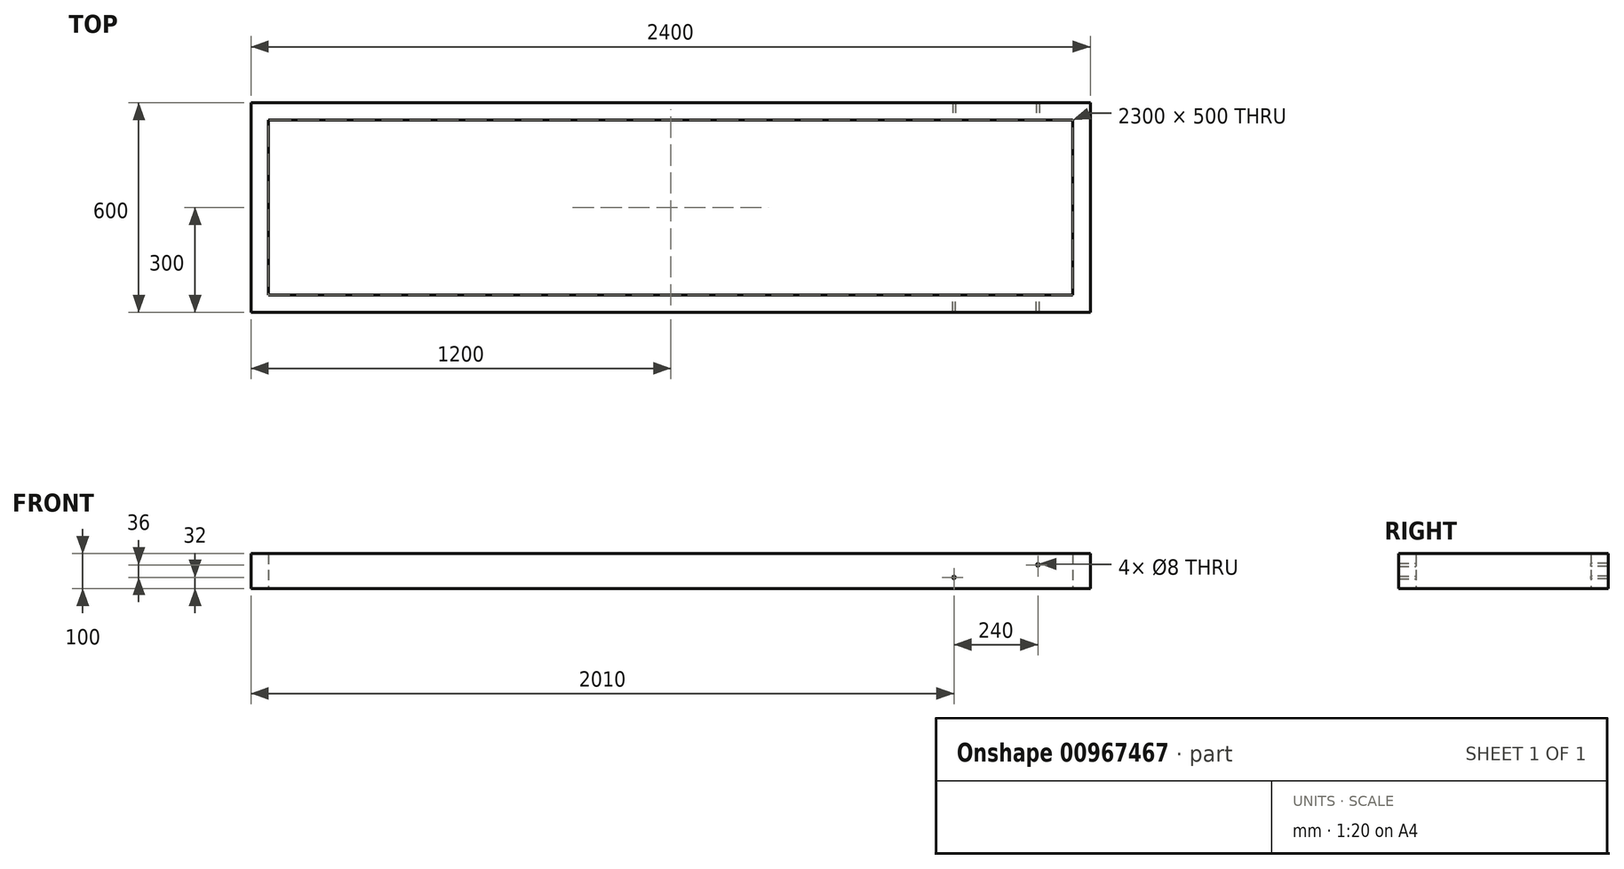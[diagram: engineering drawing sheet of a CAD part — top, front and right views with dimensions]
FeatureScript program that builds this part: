
annotation { "Feature Type Name" : "Feature", "Feature Type Description" : "" }
export const myFeature = defineFeature(function(context is Context, id is Id, definition is map)
    precondition{}
    {
        {
            var Q0;
            Q0=qCreatedBy(makeId("Top.planeOp"),FACE);
            var sketch = newSketch(context, id + "F0", { "sketchPlane" : qUnion([Q0])});
            skLineSegment(sketch, "E0.bottom", {"start": v(1200, -300) * mm, "end": v(-1200, -300) * mm});
            skLineSegment(sketch, "E0.top", {"start": v(1200, 300) * mm, "end": v(-1200, 300) * mm});
            skLineSegment(sketch, "E0.left", {"start": v(1200, -300) * mm, "end": v(1200, 300) * mm});
            skLineSegment(sketch, "E0.right", {"start": v(-1200, -300) * mm, "end": v(-1200, 300) * mm});
            skPoint(sketch, "E0.middle", {"position": v(0, 0) * mm});
            skLineSegment(sketch, "E1.bottom", {"start": v(1150, -250) * mm, "end": v(-1150, -250) * mm});
            skLineSegment(sketch, "E1.top", {"start": v(1150, 250) * mm, "end": v(-1150, 250) * mm});
            skLineSegment(sketch, "E1.left", {"start": v(1150, -250) * mm, "end": v(1150, 250) * mm});
            skLineSegment(sketch, "E1.right", {"start": v(-1150, -250) * mm, "end": v(-1150, 250) * mm});
            skSolve(sketch);
        }
        {
            var Q0;
            Q0=makeQuery(id+"F0.imprint","IMPRINT",FACE,{"disambiguationData":[TD([[makeQuery(id+"F0.imprint","IMPRINT",EDGE,{"derivedFrom":sQuery(id+"F0.wireOp",EDGE,"E0.bottom")}),-1.0]])]});
            extrude(context, id + "F1", {"entities" : qUnion([Q0]), "depth" : 100 * mm, "offsetDistance" : 25 * mm});
        }
        {
            var Q0;
            Q0=makeQuery(id+"F1.opExtrude","SWEPT_FACE",FACE,{"disambiguationData":[OSD([sQuery(id+"F0.wireOp",EDGE,"E1.top")])]});
            var sketch = newSketch(context, id + "F2", { "sketchPlane" : qUnion([Q0])});
            skCircle(sketch, "E2", {"center": v(1050, 68) * mm, "radius": 4 * mm});
            skCircle(sketch, "E3", {"center": v(810, 32) * mm, "radius": 4 * mm});
            skSolve(sketch);
        }
        {
            var Q0;
            Q0=makeQuery(id+"F2.imprint","IMPRINT",FACE,{"disambiguationData":[TD([[makeQuery(id+"F2.imprint","IMPRINT",EDGE,{"derivedFrom":sQuery(id+"F2.wireOp",EDGE,"E3")}),1.0]])]});
            var Q1;
            Q1=makeQuery(id+"F2.imprint","IMPRINT",FACE,{"disambiguationData":[TD([[makeQuery(id+"F2.imprint","IMPRINT",EDGE,{"derivedFrom":sQuery(id+"F2.wireOp",EDGE,"E2")}),1.0]])]});
            var Q2;
            Q2=makeQuery(id+"F1.opExtrude","SWEPT_FACE",FACE,{"disambiguationData":[OSD([sQuery(id+"F0.wireOp",EDGE,"E0.top")])]});
            var Q3;
            Q3=makeQuery(id+"F1.opExtrude","SWEPT_FACE",FACE,{"disambiguationData":[OSD([sQuery(id+"F0.wireOp",EDGE,"E0.bottom")])]});
            var Q4;
            Q4=makeQuery(id+"F1.opExtrude","SWEPT_BODY",BODY,{"disambiguationData":[OSD([sQuery(id+"F0.wireOp",EDGE,"E0.bottom"),sQuery(id+"F0.wireOp",EDGE,"E0.top"),sQuery(id+"F0.wireOp",EDGE,"E0.left"),sQuery(id+"F0.wireOp",EDGE,"E0.right"),sQuery(id+"F0.wireOp",EDGE,"E1.bottom"),sQuery(id+"F0.wireOp",EDGE,"E1.top"),sQuery(id+"F0.wireOp",EDGE,"E1.left"),sQuery(id+"F0.wireOp",EDGE,"E1.right")])]});
            extrude(context, id + "F3", {"entities" : qUnion([Q0, Q1]), "operationType" : NewBodyOperationType.REMOVE, "endBound" : BoundingType.UP_TO_NEXT, "oppositeDirection" : true, "depth" : 25 * mm, "endBoundEntityFace" : qUnion([Q2]), "offsetDistance" : 25 * mm});
        }
        {
            var Q0;
            Q0=makeQuery(id+"F1.opExtrude","SWEPT_FACE",FACE,{"disambiguationData":[OSD([sQuery(id+"F0.wireOp",EDGE,"E1.bottom")])]});
            var sketch = newSketch(context, id + "F4", { "sketchPlane" : qUnion([Q0])});
            skCircle(sketch, "E4", {"center": v(-1050, 68) * mm, "radius": 4 * mm});
            skCircle(sketch, "E5", {"center": v(-810, 32) * mm, "radius": 4 * mm});
            skSolve(sketch);
        }
        {
            var Q0;
            Q0=makeQuery(id+"F4.imprint","IMPRINT",FACE,{"disambiguationData":[TD([[makeQuery(id+"F4.imprint","IMPRINT",EDGE,{"derivedFrom":sQuery(id+"F4.wireOp",EDGE,"E5")}),1.0]])]});
            var Q1;
            Q1=makeQuery(id+"F4.imprint","IMPRINT",FACE,{"disambiguationData":[TD([[makeQuery(id+"F4.imprint","IMPRINT",EDGE,{"derivedFrom":sQuery(id+"F4.wireOp",EDGE,"E4")}),1.0]])]});
            extrude(context, id + "F5", {"entities" : qUnion([Q0, Q1]), "operationType" : NewBodyOperationType.REMOVE, "endBound" : BoundingType.UP_TO_NEXT, "oppositeDirection" : true, "depth" : 25 * mm, "offsetDistance" : 25 * mm});
        }
    });
